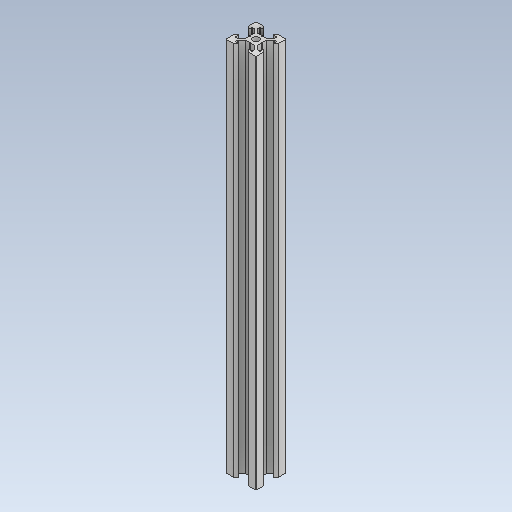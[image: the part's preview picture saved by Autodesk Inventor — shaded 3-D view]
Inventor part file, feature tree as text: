
AUTODESK INVENTOR PART (.ipt)
format: ipt  version: 2021 (Build 250183000, 183)  size: 239,616 bytes
history: native  units: mm
features: sketch x4, extrude x2, fillet x2, other x1, pattern_circular x1, hole x1, projected_geometry x1
ambient origin geometry x8: Origin, YZ Plane, XZ Plane, XY Plane, X Axis, Y Axis, Z Axis, Center Point
bodies: Body1 (feature_tree)
feature tree (12):
  other  "實體1"
  extrude  "擠出1"  Depth=20.0mm
  extrude  "擠出2"  Depth=20.0mm
  fillet  "圓角1"  Radius=250.0mm
  pattern_circular  "環形陣列1"  [2 undecoded]
  hole  "孔1"  [1 undecoded]
  fillet  "圓角2"  Radius=6.2mm
  sketch  "草圖4"
  sketch  "草圖1"
  sketch  "草圖2"
  projected_geometry  "投影迴路1"
  sketch  "草圖3"
note: 3 required parameter values undecoded (feature->parameter linkage not recoverable at this tier; creation-order binding heuristic only, values carry confidence <= 0.55)
